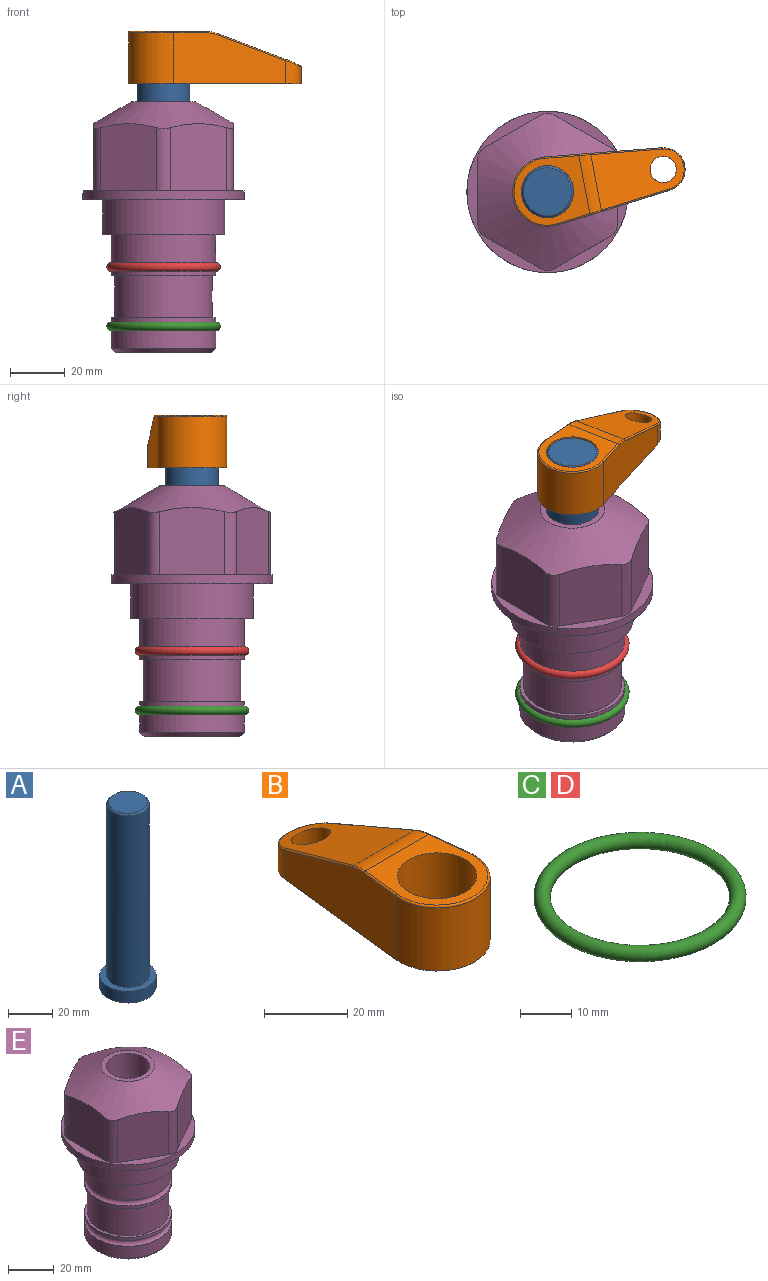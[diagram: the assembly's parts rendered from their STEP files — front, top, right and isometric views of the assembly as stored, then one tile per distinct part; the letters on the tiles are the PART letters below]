
ASSEMBLY  parts=5 mates=3
PART A: 6 faces, bbox 25.4x25.4x101.6 mm
  f0: plane 17.46x17.46mm, normal (0,0,1), area 239.5mm2, adj f5
  f1: plane 25.4x25.4mm, normal (0,0,-1), area 506.7mm2, adj f2
  f2: cylinder r=12.7mm len=25.4mm, axis (0,0,1), area 506.7mm2, adj f1,f3
  f3: plane 25.4x25.4mm, normal (0,0,1), area 221.7mm2, adj f2,f4
  f4: cylinder r=9.53mm len=94.46mm, axis (0,0,1), area 5653mm2, adj f3,f5
  f5: cone r=8.73mm half-angle=45deg, axis (0,0,-1), area 64.4mm2, adj f0,f4
PART B: 44 faces, bbox 27.5x64.5x19.1 mm
  f0: plane 2.3x0.95mm, normal (0,0,-1), area 1mm2, adj f25,f30,f34
  f1: plane 63.5x25.4mm, normal (0,0,-1), area 561.7mm2, adj f2,f3,f4,f5,f6,f7,f19,f20
  f2: cylinder r=12.7mm len=25.4mm, axis (0,0,-1), area 792.2mm2, adj f1,f3,f5,f13
  f3: plane 42.33x18.54mm, normal (0.99,0.11,0), area 647mm2, adj f1,f2,f4,f11,f12,f14
  f4: cylinder r=7.94mm len=15.78mm, axis (0,0,-1), area 158.6mm2, adj f1,f3,f5,f16
  f5: plane 42.33x18.54mm, normal (-0.99,0.11,0), area 647mm2, adj f1,f2,f4,f15,f17,f18
  f6: cylinder r=9.53mm len=19.05mm, axis (0,0,-1), area 1140.1mm2, adj f1,f8
  f7: cylinder r=4.76mm len=10.98mm, axis (0,0,-1), area 276.1mm2, adj f1,f9
  f8: plane 25.83x24.38mm, normal (0,0,1), area 262.2mm2, adj f6,f10,f11,f13,f15
  f9: plane 32.49x20.55mm, normal (0,0.34,0.94), area 489.9mm2, adj f7,f10,f14,f16,f18
  f10: cylinder r=12.7mm len=21.49mm, axis (-1,0,0), area 93.2mm2, adj f8,f9,f12,f17
  f11: cylinder r=0.51mm len=12.34mm, axis (0.11,-0.99,0), area 9.9mm2, adj f3,f8,f12,f13
  f12: bspline ~7.62x1.64mm, area 3.5mm2, adj f3,f10,f11,f14
  f13: torus R=12.19mm, axis (0,0,1), area 33.6mm2, adj f2,f8,f11,f15
  f14: cylinder r=0.51mm len=26.01mm, axis (0.1,-0.93,0.34), area 21.6mm2, adj f3,f9,f12,f16
  f15: cylinder r=0.51mm len=12.34mm, axis (0.11,0.99,0), area 9.9mm2, adj f5,f8,f13,f17
  f16: bspline ~15.78x7.05mm, area 15.7mm2, adj f4,f9,f14,f18
  f17: bspline ~7.62x1.64mm, area 3.5mm2, adj f5,f10,f15,f18
  f18: cylinder r=0.51mm len=26.01mm, axis (0.1,0.93,-0.34), area 21.6mm2, adj f5,f9,f16,f17
  f19: plane 21.6x14.29mm, normal (-0.99,-0.11,0), area 242.6mm2, adj f1,f26,f28,f34,f36,f38
  f20: plane 21.6x14.29mm, normal (0.99,-0.11,0), area 242.6mm2, adj f1,f27,f29,f37,f39,f41
  f21: cylinder r=12.7mm len=14.29mm, axis (0,0,-1), area 173.2mm2, adj f1,f26,f27,f30,f31,f33
  f22: cylinder r=7.94mm len=7.63mm, axis (0,0,-1), area 53.8mm2, adj f1,f28,f29,f42
  f23: plane 2.3x0.95mm, normal (0,0,-1), area 1mm2, adj f25,f33,f37
  f24: plane 17.94x12.32mm, normal (0,-0.34,-0.94), area 191.2mm2, adj f25,f38,f41,f42
  f25: cylinder r=9.53mm len=12.93mm, axis (-1,0,0), area 37.5mm2, adj f0,f23,f24,f31,f36,f39
  f26: cylinder r=1.59mm len=14.29mm, axis (0,0,-1), area 49mm2, adj f1,f19,f21,f32
  f27: cylinder r=1.59mm len=14.29mm, axis (0,0,-1), area 49mm2, adj f1,f20,f21,f35
  f28: cylinder r=1.59mm len=7.28mm, axis (0,0,-1), area 22.1mm2, adj f1,f19,f22,f40
  f29: cylinder r=1.59mm len=7.28mm, axis (0,0,-1), area 22.1mm2, adj f1,f20,f22,f43
  f30: torus R=14.29mm, axis (0,0,1), area 5.8mm2, adj f0,f21,f31,f32
  f31: bspline ~11.06x2.73mm, area 20.8mm2, adj f21,f25,f30,f33
  f32: sphere r=1.59mm, area 5.4mm2, adj f26,f30,f34
  f33: torus R=14.29mm, axis (0,0,1), area 5.8mm2, adj f21,f23,f31,f35
  f34: cylinder r=1.59mm len=1.68mm, axis (-0.11,0.99,0), area 2.4mm2, adj f0,f19,f32,f36
  f35: sphere r=1.59mm, area 5.4mm2, adj f27,f33,f37
  f36: bspline ~5.82x2.33mm, area 7.7mm2, adj f19,f25,f34,f38
  f37: cylinder r=1.59mm len=1.68mm, axis (0.11,0.99,0), area 2.4mm2, adj f20,f23,f35,f39
  f38: cylinder r=1.59mm len=18.33mm, axis (0.1,-0.93,0.34), area 46.7mm2, adj f19,f24,f36,f40
  f39: bspline ~5.82x2.33mm, area 7.7mm2, adj f20,f25,f37,f41
  f40: sphere r=1.59mm, area 3.6mm2, adj f28,f38,f42
  f41: cylinder r=1.59mm len=18.33mm, axis (0.1,0.93,-0.34), area 46.7mm2, adj f20,f24,f39,f43
  f42: bspline ~8.31x1.84mm, area 15.3mm2, adj f22,f24,f40,f43
  f43: sphere r=1.59mm, area 3.6mm2, adj f29,f41,f42
PART C: 1 faces, bbox 44.7x44.7x3.2 mm
  f0: torus R=19.05mm, axis (0,0,1), area 1193.9mm2
PART D: same geometry as C
PART E: 36 faces, bbox 58.7x58.7x91.2 mm
  f0: cylinder r=17.78mm len=35.56mm, axis (0,0,1), area 1670.8mm2, adj f23,f24,f31
  f1: cylinder r=19.05mm len=38.1mm, axis (0,0,1), area 1191.9mm2, adj f26,f27,f30
  f2: plane 58.66x58.66mm, normal (0,0,-1), area 1150.6mm2, adj f3,f28
  f3: cylinder r=29.33mm len=58.66mm, axis (0,0,-1), area 585.1mm2, adj f2,f4
  f4: plane 58.66x58.66mm, normal (0,0,1), area 475.9mm2, adj f3,f5,f6,f7,f8,f9,f10,f11
  f5: plane 24.5x20.32mm, normal (-0.5,0.87,0), area 562.8mm2, adj f4,f15,f16,f17
  f6: plane 24.5x20.32mm, normal (0.5,0.87,0), area 562.8mm2, adj f4,f14,f15,f17
  f7: plane 24.5x23.48mm, normal (1,0,0), area 562.8mm2, adj f4,f13,f14,f17
  f8: plane 24.5x20.32mm, normal (0.5,-0.87,0), area 562.8mm2, adj f4,f12,f13,f17
  f9: plane 24.5x20.32mm, normal (-0.5,-0.87,0), area 562.8mm2, adj f4,f11,f12,f17
  f10: plane 24.5x23.48mm, normal (-1,0,0), area 562.8mm2, adj f4,f11,f16,f17
  f11: cylinder r=5.08mm len=23.01mm, axis (0,0,-1), area 121.2mm2, adj f4,f9,f10,f17
  f12: cylinder r=5.08mm len=23.01mm, axis (0,0,-1), area 121.2mm2, adj f4,f8,f9,f17
  f13: cylinder r=5.08mm len=23.01mm, axis (0,0,-1), area 121.2mm2, adj f4,f7,f8,f17
  f14: cylinder r=5.08mm len=23.01mm, axis (0,0,-1), area 121.2mm2, adj f4,f6,f7,f17
  f15: cylinder r=5.08mm len=23.01mm, axis (0,0,-1), area 121.2mm2, adj f4,f5,f6,f17
  f16: cylinder r=5.08mm len=23.01mm, axis (0,0,-1), area 121.2mm2, adj f4,f5,f10,f17
  f17: cone r=11.73mm half-angle=60deg, axis (0,0,-1), area 2071.8mm2, adj f5,f6,f7,f8,f9,f10,f11,f12
  f18: plane 23.46x23.46mm, normal (0,0,1), area 147.4mm2, adj f17,f35
  f19: plane 34.93x34.93mm, normal (0,0,-1), area 958mm2, adj f29
  f20: cylinder r=19.05mm len=38.1mm, axis (0,0,1), area 760.1mm2, adj f21,f29
  f21: torus R=19.05mm, axis (0,0,1), area 565.3mm2, adj f20,f22
  f22: cylinder r=19.05mm len=38.1mm, axis (0,0,1), area 190mm2, adj f21,f23
  f23: plane 38.1x38.1mm, normal (0,0,1), area 146.9mm2, adj f0,f22
  f24: plane 38.1x38.1mm, normal (0,0,-1), area 146.9mm2, adj f0,f25
  f25: cylinder r=19.05mm len=38.1mm, axis (0,0,1), area 190mm2, adj f24,f26
  f26: torus R=19.05mm, axis (0,0,1), area 565.3mm2, adj f1,f25
  f27: plane 44.45x44.45mm, normal (0,0,-1), area 411.7mm2, adj f1,f28
  f28: cylinder r=22.23mm len=44.45mm, axis (0,0,1), area 1773.5mm2, adj f2,f27
  f29: cone r=19.05mm half-angle=45deg, axis (0,0,1), area 257.5mm2, adj f19,f20
  f30: cylinder r=3.17mm len=6.75mm, axis (-1,0,0), area 128mm2, adj f1,f33
  f31: cylinder r=3.17mm len=6.35mm, axis (-1,0,0), area 102.5mm2, adj f0,f33
  f32: plane 25.4x25.4mm, normal (0,0,1), area 506.7mm2, adj f33
  f33: cylinder r=12.7mm len=66.42mm, axis (0,0,-1), area 5236.2mm2, adj f30,f31,f32,f34
  f34: cone r=9.53mm half-angle=30deg, axis (0,0,-1), area 443.4mm2, adj f33,f35
  f35: cylinder r=9.53mm len=19.05mm, axis (0,0,-1), area 849mm2, adj f18,f34
PLACE A rot(axis=(0,0,1),10.9deg) t=(0,0,-12.48)mm
PLACE B rot(axis=(0,0,-1),79.1deg) t=(0,0,42.13)mm
PLACE C t=(0,0,-21.59)mm
PLACE D at identity
PLACE E at identity fixed
MATE fastened C.f0 <-> E.f0  axis (0,0,1) through (0,0,-46.1)mm
MATE cylindrical A.f2 <-> E.f0  axis (0,0,1) through (0,0,13.16)mm
MATE fastened B.f2 <-> A.f2  axis (0,0,1) through (0,0,61.18)mm
